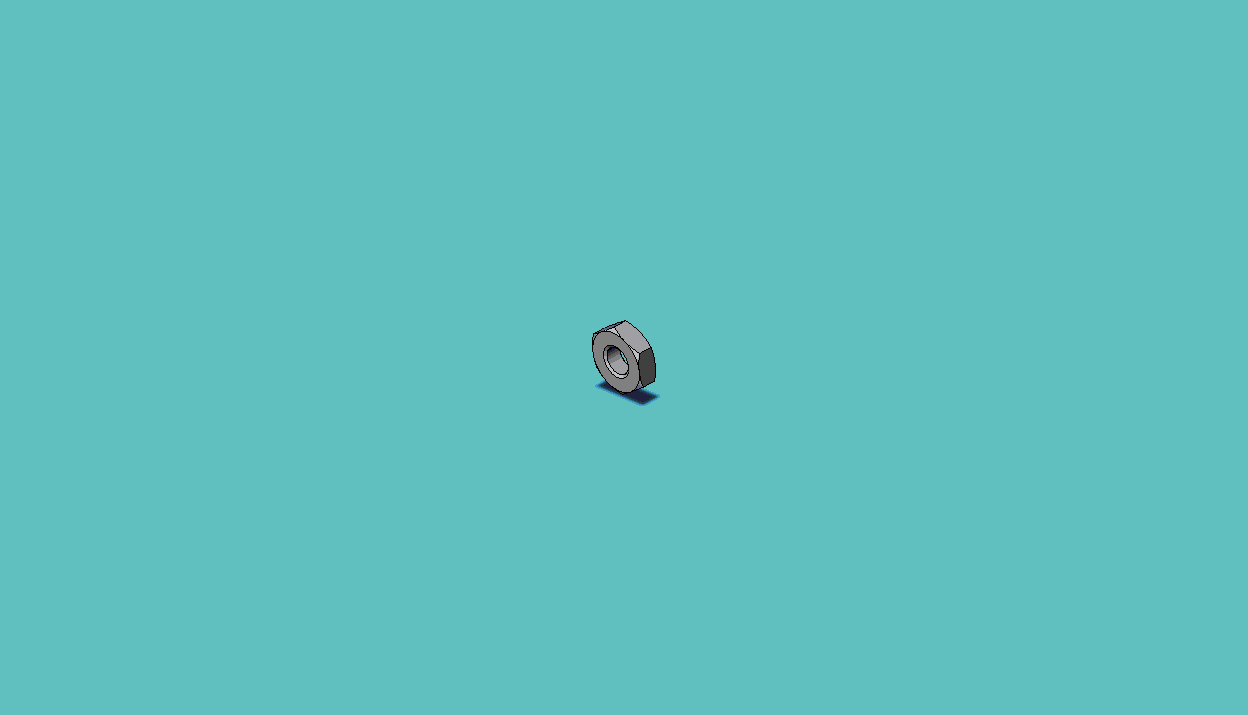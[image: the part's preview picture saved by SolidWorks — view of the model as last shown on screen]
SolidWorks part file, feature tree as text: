
SOLIDWORKS PART (.sldprt)
format: sldprt  version: not decoded by parser v0  size: 199,680 bytes
history: native  units: mm
features: sketch x4, plane x3, cut_revolve x3, material x1, extrude x1, thread x1, pattern_linear x1 + 2 further entries (+11 scaffold rows collapsed; 1 parser-record rows omitted)
feature tree (28):
  scaffold x11  (default folders/planes/origin — collapsed)
  material  "Material <not specified>"
  plane  "Plane1"
  plane  "Plane2"
  plane  "Plane3"
  parser-record x1  (decoder bookkeeping rows leaked as tree rows — omitted from the tree; the rows remain in map.json)
  cut_revolve  "EndChamfer"  [1 undecoded]
  sketch  "Sketch5"
  extrude  "BaseNut"  [1 undecoded]
  sketch  "BaseNutSke"  dims[c1.Tap_drill=2.5mm c1.D1=50.8mm c2.D1=30.0deg c2.D2=~24.797543mm c3.D2=60.0deg c3.D3=50.8mm c4.D3=30.0deg c4.D4=~24.797543mm c5.D4=60.0deg c6.D4=~24.797543mm c7.D4=60.0deg c8.D4=~24.797543mm c9.D4=60.0deg c9.Width_flats=5.5mm c9.D1=~21.475302mm c9.D2=~21.475302mm c10.D1=~21.475302mm c10.D2=2.75mm c10.D3=2.75mm c11.D1=~24.797543mm c12.D1=120.0deg c13.D1=~23.397294mm c14.D1=120.0deg c14.D4=2.75mm]
  thread  "ThreadCosmetic"  Diameter=3mm Thread_major=3mm Thickness=1.8mm  [1 undecoded]
  pattern_linear  "ThdSchPat"  [2 undecoded]
  cut_revolve  "ThreadSchematic"  [1 undecoded]
  sketch  "ThdSchSke"  dims[c1.D1=~4.490128mm c2.D1=90.0deg c3.D1=~4.490128mm c3.VeeAngle=70.0deg c4.D1=19.5834mm c4.SideAngle=55.0deg c5.D1=~4.490128mm c5.SideAngle=55.0deg c5.ThreadDepth=2.54mm c6.ThreadDepth=3.175mm c6.Thread_Major=6.35mm c6.D1=~9.573347mm c6.D2=~9.428305mm c6.OverCut=1.25mm c6.Tap_Drill=2.5mm c6.Advance=1.27mm c6.Thread_major=3.0mm c7.Advance=0.5mm c7.D1=6.35mm c7.D2=0.0254mm c8.D1=0.0254mm c9.D1=360.0deg c9.Num_threads=5.0 c9.Advance=0.4373mm c9.D2=1.0 c9.D4=50.0mm c10.D1=~8.980256mm c11.D1=315.0deg c12.D1=~8.980256mm c13.D1=45.0deg c13.D2=~8.94581mm c14.D2=~1.952549deg c14.D3=6.35mm c15.D2=25.7048mm c15.D1=~6.352235mm c16.D1=35.0deg c16.D2=12.7mm c16.D3=12.7mm c17.D2=22.5552mm c17.D3=25.4mm c17.D4=12.7mm c18.D3=12.7mm c18.D2=0.0508mm c18.Offset1=25.4254mm c18.ThreadMajor=12.7mm c18.ChamferDepth=0.275mm c18.Offset2=1.8762mm c19.ThreadMajor=1.5mm c19.Offset1=1.8254mm c19.D1=360.0deg]
  sketch  "Sketch3"  dims[c1.D1=2.75mm c1.D2=2.4mm c1.D3=12.7mm c1.D4=10.0mm c1.D5=10.9093mm c1.D6=~10.998523mm c2.D6=~179.413404deg c3.D6=~2.539714mm c3.D3=10.0mm c3.D5=9.525mm c3.D2=~10.392305mm c4.D2=30.0deg]
  cut_revolve  "Double-Chamfer"  Angle=360deg
  "ConfigurationName"  CopiedFlag=1
  "ConfigurationName"  CopiedFlag=0
decode coverage: 5 of 10 modeling features carry decoded parameters; 2 rows unclassified (native names shown)
note: ~ marks probable driven/reference dimensions
note: 6 parameter values undecoded
summary: no parameter record found for 3 features
note: suppression state not decoded; provenance and decode notes live in map.json
